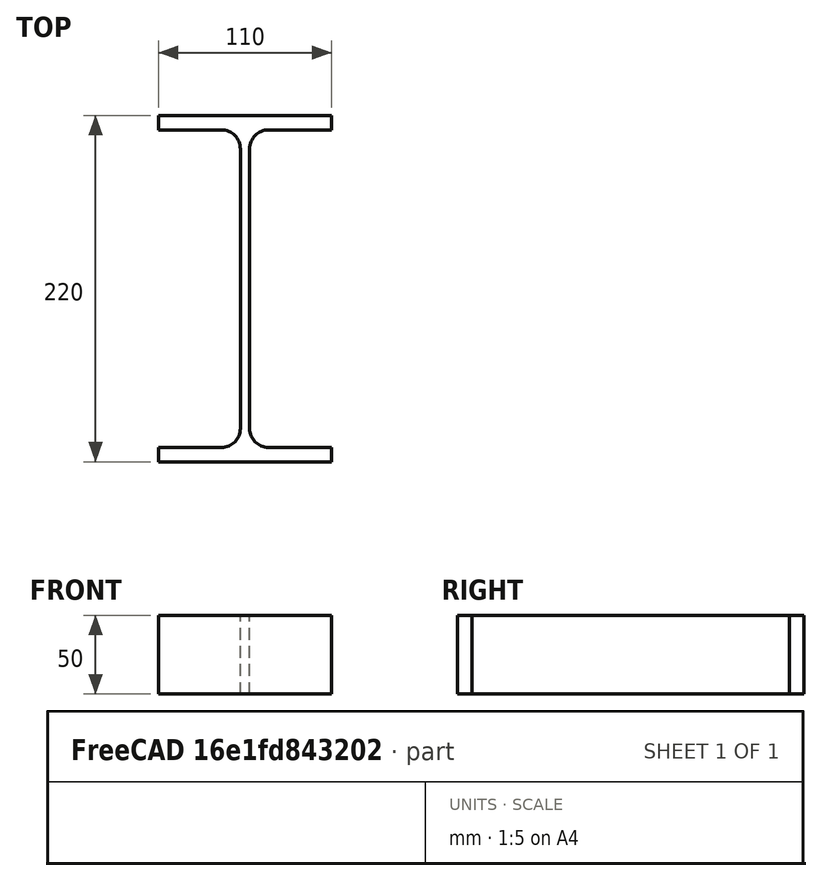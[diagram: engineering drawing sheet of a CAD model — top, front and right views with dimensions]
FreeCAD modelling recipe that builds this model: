
FCSTD DOCUMENT  (FreeCAD 0.15R4671 (Git))
Label: IPE-Profile 220 DIN1025-5 S235JR
License: All rights reserved
LicenseURL: http://en.wikipedia.org/wiki/All_rights_reserved
objects: Sketcher::SketchObject×1, Part::Extrusion×1
note: 2 computed .brp shape members not serialized (recipe doc carries the construction recipe); baked Part::Feature solids carry a one-line shape summary decoded from their .brp

FEATURE [Sketcher::SketchObject] Sketch
  sketch-geometry (16):
    g0: LineSegment StartX=2.95 StartY=-88.8 StartZ=0 EndX=2.95 EndY=88.8 EndZ=0
    g1: LineSegment StartX=14.95 StartY=100.8 StartZ=0 EndX=55 EndY=100.8 EndZ=0
    g2: LineSegment StartX=55 StartY=100.8 StartZ=0 EndX=55 EndY=110 EndZ=0
    g3: LineSegment StartX=55 StartY=110 StartZ=0 EndX=-55 EndY=110 EndZ=0
    g4: LineSegment StartX=-55 StartY=110 StartZ=0 EndX=-55 EndY=100.8 EndZ=0
    g5: LineSegment StartX=-55 StartY=100.8 StartZ=0 EndX=-14.95 EndY=100.8 EndZ=0
    g6: LineSegment StartX=-2.95 StartY=88.8 StartZ=0 EndX=-2.95 EndY=-88.8 EndZ=0
    g7: LineSegment StartX=-14.95 StartY=-100.8 StartZ=0 EndX=-55 EndY=-100.8 EndZ=0
    g8: LineSegment StartX=-55 StartY=-100.8 StartZ=0 EndX=-55 EndY=-110 EndZ=0
    g9: LineSegment StartX=-55 StartY=-110 StartZ=0 EndX=55 EndY=-110 EndZ=0
    g10: LineSegment StartX=55 StartY=-110 StartZ=0 EndX=55 EndY=-100.8 EndZ=0
    g11: LineSegment StartX=55 StartY=-100.8 StartZ=0 EndX=14.95 EndY=-100.8 EndZ=0
    g12: ArcOfCircle CenterX=14.95 CenterY=88.8 CenterZ=0 NormalX=0 NormalY=0 NormalZ=1 Radius=12 StartAngle=1.5708 EndAngle=3.14159
    g13: ArcOfCircle CenterX=14.95 CenterY=-88.8 CenterZ=0 NormalX=0 NormalY=0 NormalZ=1 Radius=12 StartAngle=3.14159 EndAngle=4.71239
    g14: ArcOfCircle CenterX=-14.95 CenterY=88.8 CenterZ=0 NormalX=0 NormalY=0 NormalZ=1 Radius=12 StartAngle=0 EndAngle=1.5708
    g15: ArcOfCircle CenterX=-14.95 CenterY=-88.8 CenterZ=0 NormalX=0 NormalY=0 NormalZ=1 Radius=12 StartAngle=4.71239 EndAngle=6.28319
  constraints (42):
    c: Vertical(g0)
    c: Coincident(g2,g1)
    c: Vertical(g2)
    c: Coincident(g3,g2)
    c: Coincident(g4,g3)
    c: Vertical(g4)
    c: Coincident(g5,g4)
    c: Horizontal(g5)
    c: Vertical(g6)
    c: Horizontal(g7)
    c: Coincident(g8,g7)
    c: Vertical(g8)
    c: Coincident(g9,g8)
    c: Horizontal(g9)
    c: Coincident(g10,g9)
    c: Vertical(g10)
    c: Coincident(g11,g10)
    c: Horizontal(g11)
    c: Tangent(g1,g12) = 1.5708
    c: Tangent(g0,g12) = 1.5708
    c: Tangent(g0,g13) = 1.5708
    c: Tangent(g11,g13) = 1.5708
    c: Tangent(g5,g14) = 1.5708
    c: Tangent(g6,g14) = 1.5708
    c: Tangent(g6,g15) = 1.5708
    c: Tangent(g7,g15) = 1.5708
    c: Equal(g3,g9)
    c: Equal(g2,g4)
    c: Equal(g4,g8)
    c: Equal(g8,g10)
    c: Equal(g12,g14)
    c: Equal(g14,g15)
    c: Equal(g15,g13)
    c: Symmetric(g2,g3,g-2)
    c: Symmetric(g9,g8,g-2)
    c: Symmetric(g0,g6,g-2)
    c: Symmetric(g2,g9,g-1)
    c: DistanceY(g2,g9) = -220
    c: DistanceX(g3) = -110
    c: DistanceX(g0,g6) = -5.9
    c: DistanceY(g2) = 9.2
    c: Radius(g12) = 12
FEATURE [Part::Extrusion] Extrude  label="IPE-Profile 220 DIN1025-5 S235JR"
  Base = -> Sketch
  Dir = (0,0,50)
  Solid = true
